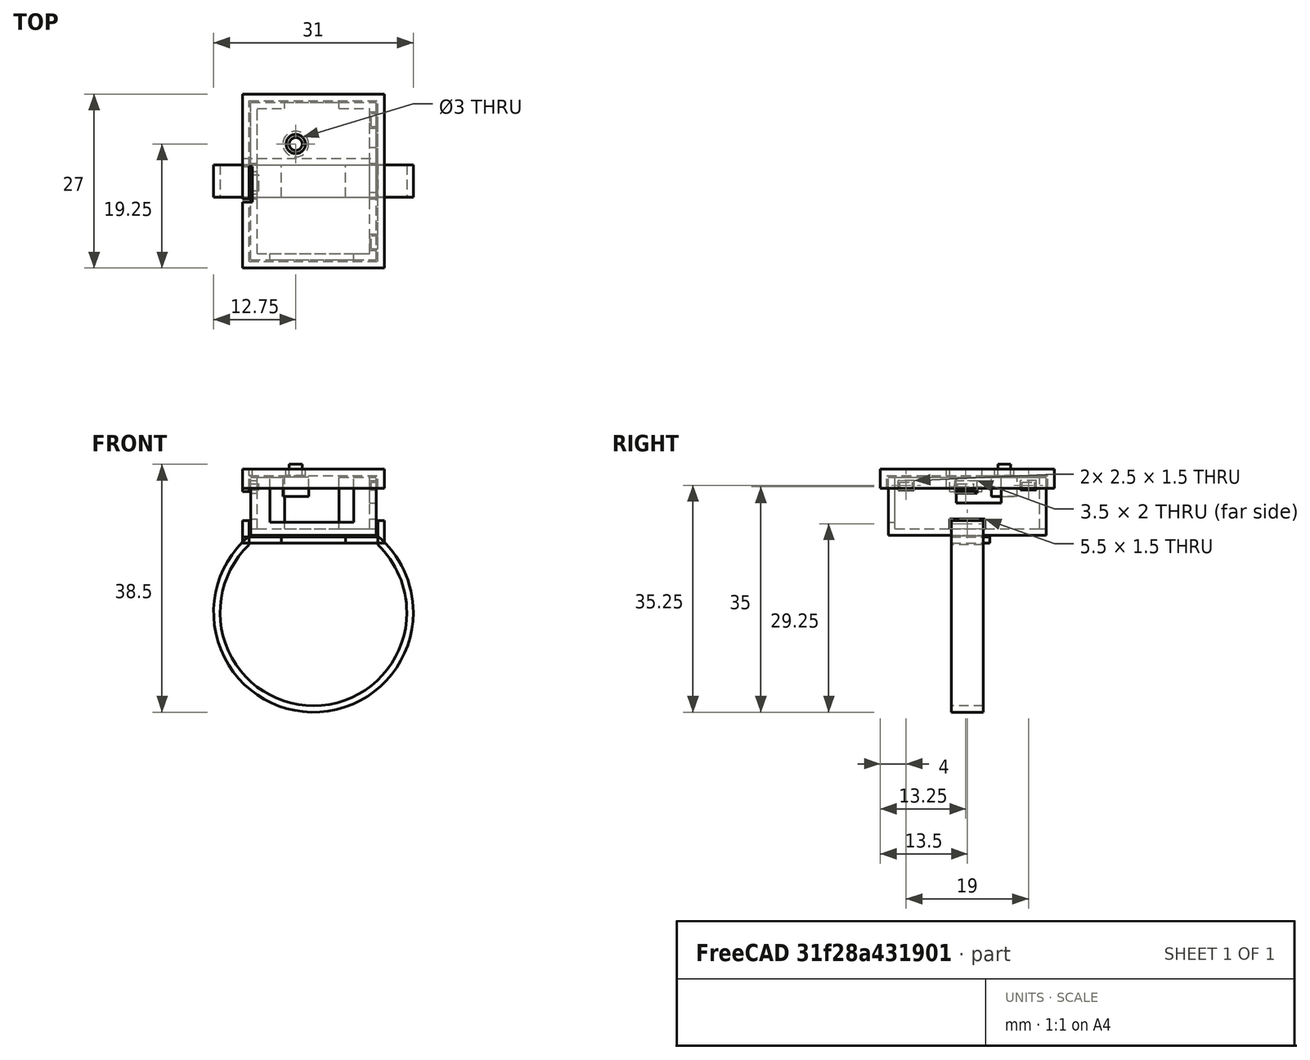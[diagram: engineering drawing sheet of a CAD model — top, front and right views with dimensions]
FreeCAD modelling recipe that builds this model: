
FCSTD DOCUMENT  (FreeCAD 0.18R16131 (Git))
Label: led_bauble_board_case
License: All rights reserved
LicenseURL: http://en.wikipedia.org/wiki/All_rights_reserved
objects: Part::Box×23, Part::Cut×14, Part::Cylinder×5, Part::MultiFuse×4
note: 46 computed .brp shape members not serialized (recipe doc carries the construction recipe); baked Part::Feature solids carry a one-line shape summary decoded from their .brp

FEATURE [Part::Box] Box  label="Cube(inner)"
  AttacherType = Attacher::AttachEngine3D
  Height = 8
  Length = 17.5
  Placement = pos=(1,0,1) rot=(0,0,1;0rad)
  Width = 22.5
FEATURE [Part::Box] Box001  label="Cube001(outer)"
  AttacherType = Attacher::AttachEngine3D
  Height = 9
  Length = 19.5
  Placement = pos=(0,-1,0) rot=(0,0,1;0rad)
  Width = 24.5
FEATURE [Part::Box] Box002  label="Cube002(port_end_hole)"
  AttacherType = Attacher::AttachEngine3D
  Height = 8
  Length = 8.5
  Placement = pos=(5.25,22.5,1) rot=(0,0,1;0rad)
  Width = 1
FEATURE [Part::Box] Box003  label="Cube003(usb_hole)"
  AttacherType = Attacher::AttachEngine3D
  Height = 7
  Length = 13
  Placement = pos=(3,-1,2) rot=(0,0,1;0rad)
  Width = 1
FEATURE [Part::Box] Box004  label="Cube004(switch_hole)"
  AttacherType = Attacher::AttachEngine3D
  Height = 4
  Length = 1
  Placement = pos=(18.5,9.5,5) rot=(0,0,1;0rad)
  Width = 7
FEATURE [Part::Box] Box005  label="Cube(inner)001"
  AttacherType = Attacher::AttachEngine3D
  Height = 2
  Length = 20
  Placement = pos=(-0.25,-1.25,7.25) rot=(0,0,1;0rad)
  Width = 25
FEATURE [Part::Box] Box006  label="Cube001(outer)001"
  AttacherType = Attacher::AttachEngine3D
  Height = 3
  Length = 22
  Placement = pos=(-1.25,-2.25,7.25) rot=(0,0,1;0rad)
  Width = 27
FEATURE [Part::Box] Box010  label="Cube004(tab_right)"
  AttacherType = Attacher::AttachEngine3D
  Height = 1
  Length = 1
  Placement = pos=(18.75,19.75,7.25) rot=(0,0,1;0rad)
  Width = 2
FEATURE [Part::Box] Box011  label="Cube005(tab_left)"
  AttacherType = Attacher::AttachEngine3D
  Height = 1
  Length = 1
  Placement = pos=(18.75,0.75,7.25) rot=(0,0,1;0rad)
  Width = 2
FEATURE [Part::Box] Box012  label="Cube004(tab_right_hole)"
  AttacherType = Attacher::AttachEngine3D
  Height = 1.5
  Length = 2
  Placement = pos=(18.25,19.5,7) rot=(0,0,1;0rad)
  Width = 2.5
FEATURE [Part::Box] Box013  label="Cube005(tab_left_hole)"
  AttacherType = Attacher::AttachEngine3D
  Height = 1.5
  Length = 2
  Placement = pos=(18.25,0.5,7) rot=(0,0,1;0rad)
  Width = 2.5
FEATURE [Part::Box] Box014  label="Cube004(clip)"
  AttacherType = Attacher::AttachEngine3D
  Height = 3.5
  Length = 1
  Placement = pos=(-1.25,8.5,6.75) rot=(0,0,1;0rad)
  Width = 5
FEATURE [Part::Box] Box015  label="Cube005(clip_cutter)"
  AttacherType = Attacher::AttachEngine3D
  Height = 3
  Length = 1.5
  Placement = pos=(-1.25,8,7.25) rot=(0,0,1;0rad)
  Width = 5.5
FEATURE [Part::Box] Box016  label="Cube006(clip_nube)"
  AttacherType = Attacher::AttachEngine3D
  Height = 1
  Length = 1.5
  Placement = pos=(-0.25,9.75,7) rot=(0,0,1;0rad)
  Width = 2.5
FEATURE [Part::Box] Box017  label="Cube006(clip_nube_hole)"
  AttacherType = Attacher::AttachEngine3D
  Height = 2
  Length = 1
  Placement = pos=(0,9.25,6.5) rot=(0,0,1;0rad)
  Width = 3.5
FEATURE [Part::Cut] Cut
  Base = -> Box001
  Tool = -> Box
FEATURE [Part::Cut] Cut010
  Base = -> Cut
  Tool = -> Box003
FEATURE [Part::Cut] Cut011
  Base = -> Cut010
  Tool = -> Box002
FEATURE [Part::Cut] Cut012
  Base = -> Cut011
  Tool = -> Box004
FEATURE [Part::Cut] Cut016
  Base = -> Box006
  Tool = -> Box005
FEATURE [Part::Cylinder] Cylinder001  label="Cylinder001(button_hole)"
  Angle = 360
  AttacherType = Attacher::AttachEngine3D
  Height = 10
  Placement = pos=(7,17,2) rot=(0,0,1;0rad)
  Radius = 1.5
FEATURE [Part::Cylinder] Cylinder002  label="Cylinder001"
  Angle = 360
  AttacherType = Attacher::AttachEngine3D
  Height = 3
  Placement = pos=(7,17,8) rot=(0,0,1;0rad)
  Radius = 1
FEATURE [Part::Cylinder] Cylinder003  label="Cylinder002"
  Angle = 360
  AttacherType = Attacher::AttachEngine3D
  Height = 3
  Placement = pos=(7,17,6) rot=(0,0,1;0rad)
  Radius = 2
FEATURE [Part::Cut] Cut019
  Base = -> Cut012
  Tool = -> Box012
FEATURE [Part::Cut] Cut020
  Base = -> Cut019
  Tool = -> Box013
FEATURE [Part::Cut] Cut021
  Base = -> Cut020
  Tool = -> Box017
FEATURE [Part::MultiFuse] Fusion
  Shapes = -> [Cut016,Box010,Box011]
FEATURE [Part::Cut] Cut022
  Base = -> Fusion
  Tool = -> Box015
FEATURE [Part::MultiFuse] Fusion001
  Shapes = -> [Box016,Box014,Cut022]
FEATURE [Part::Cut] Cut023
  Base = -> Fusion001
  Tool = -> Cylinder001
FEATURE [Part::Box] Box019  label="Cube004(ring_notch_hole)"
  AttacherType = Attacher::AttachEngine3D
  Height = 1.5
  Length = 1
  Placement = pos=(0,8.5,1) rot=(0,0,1;0rad)
  Width = 5.5
FEATURE [Part::Box] Box020  label="Cube004(ring_notch)"
  AttacherType = Attacher::AttachEngine3D
  Height = 1
  Length = 5
  Placement = pos=(-0.25,8.75,-1.2) rot=(0,0,1;0rad)
  Width = 5
FEATURE [Part::Box] Box021  label="Cube004(ring_base)"
  AttacherType = Attacher::AttachEngine3D
  Height = 1
  Length = 21
  Placement = pos=(-1.25,8.75,-1.25) rot=(0,0,1;0rad)
  Width = 6
FEATURE [Part::Box] Box022  label="Cube004(ring_base_side_notch)"
  AttacherType = Attacher::AttachEngine3D
  Height = 3.5
  Length = 1
  Placement = pos=(-1.25,8.75,-1.25) rot=(0,0,1;0rad)
  Width = 5
FEATURE [Part::Box] Box023  label="Cube004(ring_base_side_clip)"
  AttacherType = Attacher::AttachEngine3D
  Height = 3.5
  Length = 1
  Placement = pos=(19.75,8.75,-1.25) rot=(0,0,1;0rad)
  Width = 5
FEATURE [Part::Box] Box024  label="Cube004(ring_clip_hole)"
  AttacherType = Attacher::AttachEngine3D
  Height = 1.5
  Length = 1
  Placement = pos=(18.5,8.5,1) rot=(0,0,1;0rad)
  Width = 5.5
FEATURE [Part::Cut] Cut025
  Base = -> Cut021
  Tool = -> Box019
FEATURE [Part::MultiFuse] Fusion002  label="Fusion002(button)"
  Shapes = -> [Cylinder002,Cylinder003]
FEATURE [Part::Cylinder] Cylinder004  label="Cylinder003(outer"
  Angle = 360
  AttacherType = Attacher::AttachEngine3D
  Height = 5
  Placement = pos=(9.75,13.75,-12) rot=(1,0,0;1.5708rad)
  Radius = 15.5
FEATURE [Part::Cylinder] Cylinder005  label="Cylinder004(inner)"
  Angle = 360
  AttacherType = Attacher::AttachEngine3D
  Height = 5
  Placement = pos=(9.75,13.75,-12) rot=(1,0,0;1.5708rad)
  Radius = 14.5
FEATURE [Part::Box] Box027  label="Cube004(ring_cutter)"
  AttacherType = Attacher::AttachEngine3D
  Height = 10
  Length = 20
  Placement = pos=(-0.25,8.75,-2) rot=(0,0,1;0rad)
  Width = 5
FEATURE [Part::Cut] Cut027
  Base = -> Cylinder004
  Tool = -> Cylinder005
FEATURE [Part::Cut] Cut028
  Base = -> Cut027
  Tool = -> Box027
FEATURE [Part::Box] Box028  label="Cube004(ring_notch)001"
  AttacherType = Attacher::AttachEngine3D
  Height = 1
  Length = 5
  Placement = pos=(14.75,8.75,-1.2) rot=(0,0,1;0rad)
  Width = 5
FEATURE [Part::Cut] Cut029
  Base = -> Cut025
  Tool = -> Box024
FEATURE [Part::MultiFuse] Fusion003
  Shapes = -> [Cut028,Box028,Box020]
